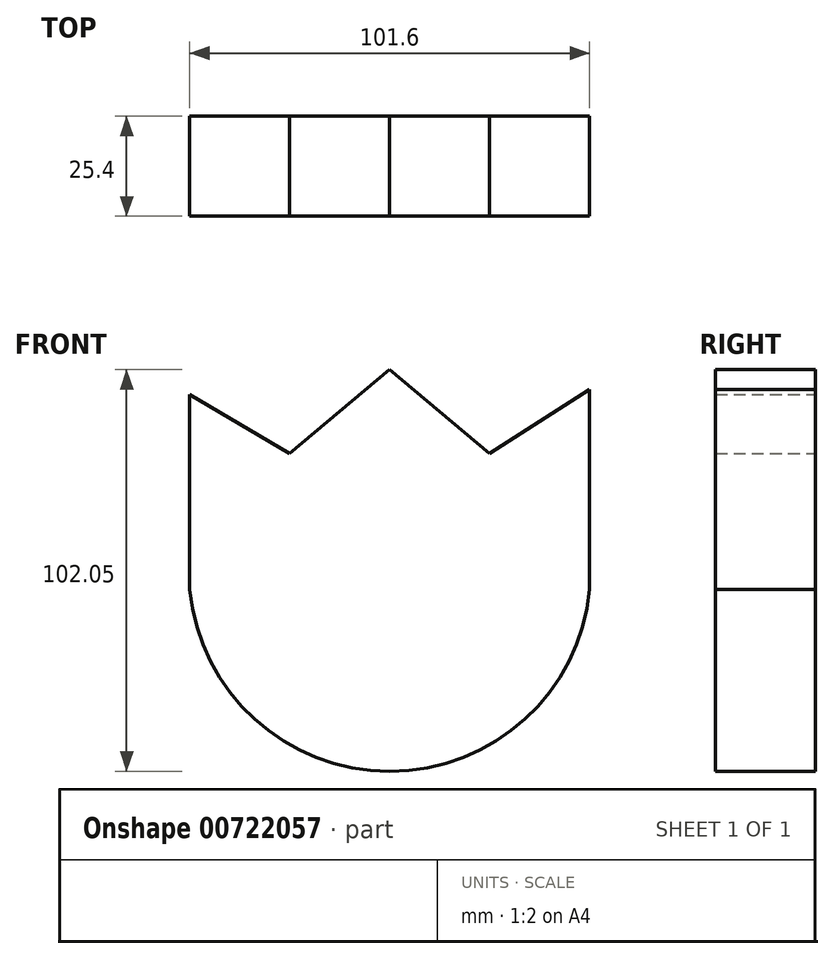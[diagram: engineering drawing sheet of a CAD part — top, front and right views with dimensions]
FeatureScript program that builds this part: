
annotation { "Feature Type Name" : "Feature", "Feature Type Description" : "" }
export const myFeature = defineFeature(function(context is Context, id is Id, definition is map)
    precondition{}
    {
        {
            var Q0;
            Q0=qCreatedBy(makeId("Front.planeOp"),FACE);
            var sketch = newSketch(context, id + "F0", { "sketchPlane" : qUnion([Q0])});
            skArc(sketch, "E0", {"start": v(-50.8, 0) * mm, "mid": v(0, -46.23) * mm, "end": v(50.8, 0) * mm});
            skPoint(sketch, "E1.start.orphan", {"position": v(-10.41, 16.45) * mm});
            skPoint(sketch, "E2.start.orphan", {"position": v(0, 45.65) * mm});
            skPoint(sketch, "E3.end.orphan", {"position": v(10.41, 16.45) * mm});
            skLineSegment(sketch, "E4", {"start": v(50.8, 0) * mm, "end": v(50.8, 50.8) * mm});
            skLineSegment(sketch, "E5", {"start": v(-50.8, 0) * mm, "end": v(-50.8, 49.54) * mm});
            skPoint(sketch, "E6", {"position": v(24.17, 30.04) * mm});
            skLineSegment(sketch, "E7", {"start": v(50.8, 50.8) * mm, "end": v(25.4, 34.47) * mm});
            skLineSegment(sketch, "E8", {"start": v(-25.4, 34.47) * mm, "end": v(-50.8, 49.54) * mm});
            skPoint(sketch, "E9.start.orphan", {"position": v(-50.8, 30.04) * mm});
            skPoint(sketch, "E10.end.orphan", {"position": v(50.8, 30.04) * mm});
            skPoint(sketch, "E11.end.orphan", {"position": v(50.8, 34.47) * mm});
            skPoint(sketch, "E12.end.orphan", {"position": v(0, 53.86) * mm});
            skLineSegment(sketch, "E13", {"start": v(0, 55.82) * mm, "end": v(25.4, 34.47) * mm});
            skLineSegment(sketch, "E14", {"start": v(0, 55.82) * mm, "end": v(-25.4, 34.47) * mm});
            skPoint(sketch, "E15.end.orphan", {"position": v(-50.8, 34.47) * mm});
            skSolve(sketch);
        }
        {
            var Q0;
            Q0=qSketchRegion(id+"F0",true);
            extrude(context, id + "F1", {"entities" : qUnion([Q0]), "depth" : 25.4 * mm, "offsetDistance" : 25.4 * mm});
        }
    });
